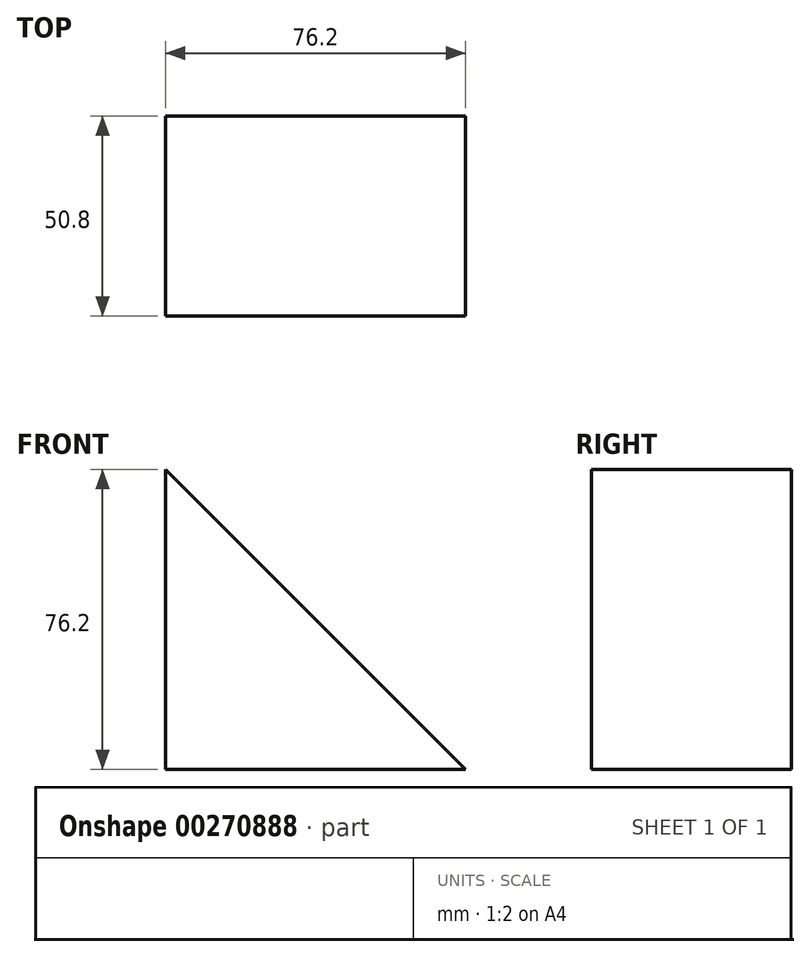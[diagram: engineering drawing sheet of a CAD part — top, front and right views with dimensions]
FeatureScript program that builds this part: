
annotation { "Feature Type Name" : "Feature", "Feature Type Description" : "" }
export const myFeature = defineFeature(function(context is Context, id is Id, definition is map)
    precondition{}
    {
        {
            var Q0;
            Q0=qCreatedBy(makeId("Front.planeOp"),FACE);
            var sketch = newSketch(context, id + "F0", { "sketchPlane" : qUnion([Q0])});
            skLineSegment(sketch, "E0", {"start": v(0, 0) * mm, "end": v(-76.2, 0) * mm});
            skLineSegment(sketch, "E1", {"start": v(-76.2, 0) * mm, "end": v(-76.2, 76.2) * mm});
            skLineSegment(sketch, "E2", {"start": v(-76.2, 76.2) * mm, "end": v(0, 0) * mm});
            skSolve(sketch);
        }
        {
            var Q0;
            Q0 = qSketchRegion(id + "F0", true);
            extrude(context, id + "F1", {"entities" : qUnion([Q0]), "depth" : 50.8 * mm});
        }
    });
